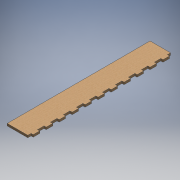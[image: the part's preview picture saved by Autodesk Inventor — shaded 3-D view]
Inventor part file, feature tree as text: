
AUTODESK INVENTOR PART (.ipt)
format: ipt  version: 2016 (Build 200138000, 138)  size: 177,664 bytes
history: native  units: mm
features: extrude x1, sketch x1
ambient origin geometry x8: Origin, YZ Plane, XZ Plane, XY Plane, X Axis, Y Axis, Z Axis, Center Point
bodies: Body1 (feature_tree)
feature tree (2):
  extrude  "Extrusion5"  Depth=6.39mm
  sketch  "Sketch2"  dims[d56=18.958829mm d58=6.39mm d70=110.0mm d72=37.917659mm d73=10.0mm d75=10.0mm d77=60.0mm d78=9.479415mm d79=9.479415mm d80=417.094246mm d94=6.39mm d95=0.0mm]
